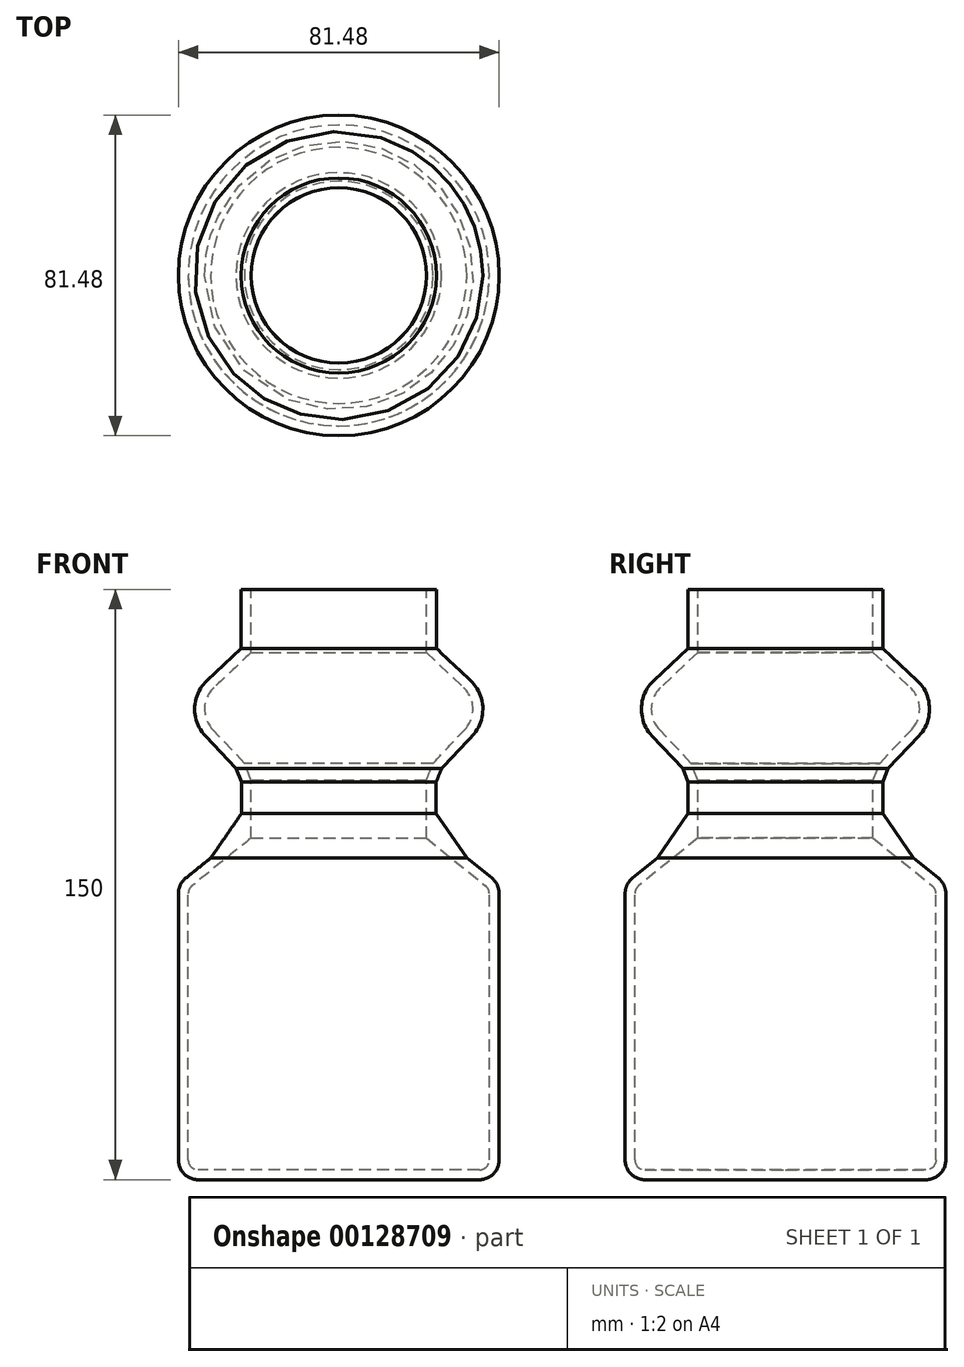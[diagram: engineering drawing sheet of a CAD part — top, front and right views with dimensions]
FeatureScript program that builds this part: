
annotation { "Feature Type Name" : "Feature", "Feature Type Description" : "" }
export const myFeature = defineFeature(function(context is Context, id is Id, definition is map)
    precondition{}
    {
        {
            var Q0;
            Q0=qCreatedBy(makeId("Front.planeOp"),FACE);
            var sketch = newSketch(context, id + "F0", { "sketchPlane" : qUnion([Q0])});
            skLineSegment(sketch, "E0", {"start": v(0, 0) * mm, "end": v(40.74, 0) * mm});
            skLineSegment(sketch, "E1", {"start": v(40.74, 0) * mm, "end": v(40.74, 75.1) * mm});
            skLineSegment(sketch, "E2", {"start": v(40.74, 75.1) * mm, "end": v(24.74, 87.99) * mm});
            skLineSegment(sketch, "E3", {"start": v(24.74, 87.99) * mm, "end": v(24.74, 102.99) * mm});
            skLineSegment(sketch, "E4", {"start": v(24.74, 102.99) * mm, "end": v(40.74, 120) * mm});
            skLineSegment(sketch, "E5", {"start": v(40.74, 120) * mm, "end": v(24.78, 135) * mm});
            skLineSegment(sketch, "E6", {"start": v(24.78, 135) * mm, "end": v(24.78, 150) * mm});
            skLineSegment(sketch, "E7", {"start": v(24.78, 150) * mm, "end": v(0, 150) * mm});
            skLineSegment(sketch, "E8", {"start": v(0, 150) * mm, "end": v(0, 0) * mm});
            skSolve(sketch);
        }
        {
            var Q0;
            Q0 = qSketchRegion(id + "F0", true);
            var Q1;
            Q1=sQuery(id+"F0.wireOp",EDGE,"E8");
            revolve(context, id + "F1", {"entities" : qUnion([Q0]), "axis" : qUnion([Q1]), "revolveType" : RevolveType.FULL});
        }
        {
            var Q0;
            Q0=makeQuery(id+"F1.opRevolve","SWEPT_EDGE",EDGE,{"disambiguationData":[OSD([sQuery(id+"F0.wireOp",EDGE,"E0"),sQuery(id+"F0.wireOp",EDGE,"E1")])]});
            fillet(context, id + "F2", {"entities" : qUnion([Q0]), "radius" : 5 * mm, "tangentPropagation" : true, "allowEdgeOverflow" : false});
        }
        {
            var Q0;
            Q0=makeQuery(id+"F1.opRevolve","SWEPT_EDGE",EDGE,{"disambiguationData":[OSD([sQuery(id+"F0.wireOp",EDGE,"E4"),sQuery(id+"F0.wireOp",EDGE,"E5")])]});
            fillet(context, id + "F3", {"entities" : qUnion([Q0]), "radius" : 10 * mm, "tangentPropagation" : true, "allowEdgeOverflow" : false});
        }
        {
            var Q0;
            Q0=makeQuery(id+"F1.opRevolve","SWEPT_EDGE",EDGE,{"disambiguationData":[OSD([sQuery(id+"F0.wireOp",EDGE,"E3"),sQuery(id+"F0.wireOp",EDGE,"E4")])]});
            chamfer(context, id + "F4", {"entities" : qUnion([Q0]), "width" : 5 * mm, "tangentPropagation" : true});
        }
        {
            var Q0;
            Q0=makeQuery(id+"F1.opRevolve","SWEPT_EDGE",EDGE,{"disambiguationData":[OSD([sQuery(id+"F0.wireOp",EDGE,"E1"),sQuery(id+"F0.wireOp",EDGE,"E2")])]});
            fillet(context, id + "F5", {"entities" : qUnion([Q0]), "radius" : 5 * mm, "tangentPropagation" : true, "allowEdgeOverflow" : false});
        }
        {
            var Q0;
            Q0=makeQuery(id+"F1.opRevolve","SWEPT_FACE",FACE,{"disambiguationData":[OSD([sQuery(id+"F0.wireOp",EDGE,"E7")])]});
            shell(context, id + "F6", {"entities" : qUnion([Q0]), "thickness" : 2.5 * mm});
        }
        {
            var Q0;
            Q0=makeQuery(id+"F1.opRevolve","SWEPT_EDGE",EDGE,{"disambiguationData":[OSD([sQuery(id+"F0.wireOp",EDGE,"E2"),sQuery(id+"F0.wireOp",EDGE,"E3")])]});
            chamfer(context, id + "F7", {"entities" : qUnion([Q0]), "chamferType" : ChamferType.TWO_OFFSETS, "width1" : 5 * mm, "oppositeDirection" : false, "width2" : 10 * mm, "tangentPropagation" : true});
        }
    });
